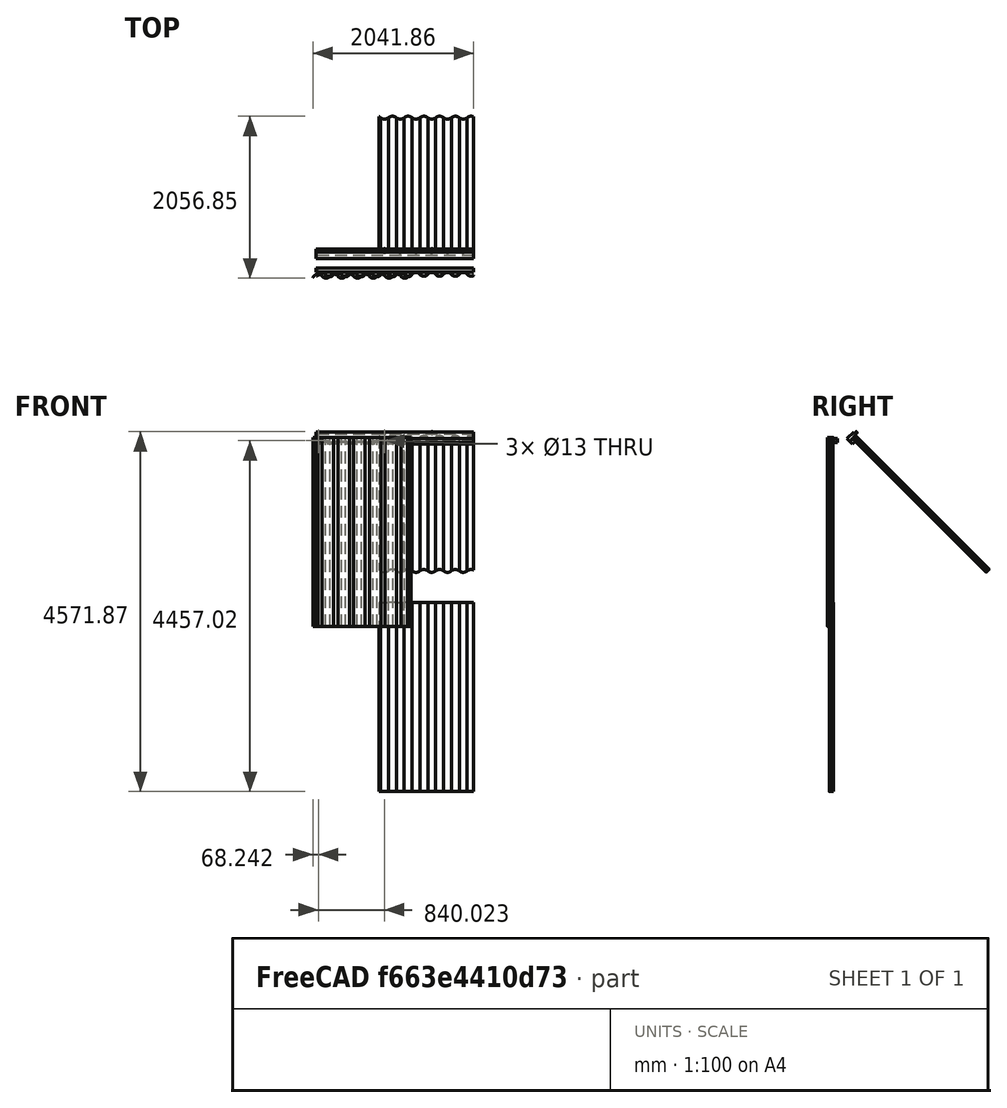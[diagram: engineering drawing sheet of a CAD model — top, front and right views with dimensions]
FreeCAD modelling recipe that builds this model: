
FCSTD DOCUMENT  (FreeCAD 0.17R11732 (Git))
Label: telhas
License: All rights reserved
LicenseURL: http://en.wikipedia.org/wiki/All_rights_reserved
objects: Part::FeaturePython×29, Part::Mirroring×3, App::FeaturePython×2, Part::Part2DObjectPython×2, Part::Feature×1, Part::Sweep×1
note: 36 computed .brp shape members not serialized (recipe doc carries the construction recipe); baked Part::Feature solids carry a one-line shape summary decoded from their .brp

FEATURE [Part::FeaturePython] Panel  # WARN: FeaturePython — macro-defined, semantics opaque (R4)
  Area = 2880000
  FaceMaker = 0
  HorizontalArea = 0
  Length = 1200
  MoveWithHost = false
  Normal = (0,0,0)
  PerimeterLength = 0
  Placement = pos=(-841.859,-100,-100) rot=(1,0,0;1.5708rad)
  Role = 0
  Sheets = 1
  Thickness = 5
  VerticalArea = 0
  WaveDirection = 0
  WaveHeight = 25
  WaveLength = 100
  WaveType = 0
  Width = 2400
FEATURE [Part::FeaturePython] Panel001  # WARN: FeaturePython — macro-defined, semantics opaque (R4)
  Area = 2880000
  CloneOf = -> Panel
  FaceMaker = 0
  HorizontalArea = 0
  Length = 1200
  MoveWithHost = false
  Normal = (0,0,0)
  PerimeterLength = 0
  Placement = pos=(-795.762,-82.2313,-100) rot=(1,0,0;1.5708rad)
  Role = 0
  Sheets = 1
  Thickness = 5
  VerticalArea = 0
  WaveDirection = 0
  WaveHeight = 0
  WaveLength = 0
  WaveType = 0
  Width = 2400
FEATURE [Part::FeaturePython] Panel002  # WARN: FeaturePython — macro-defined, semantics opaque (R4)
  Area = 2880000
  CloneOf = -> Panel
  FaceMaker = 0
  HorizontalArea = 0
  Length = 1200
  MoveWithHost = false
  Normal = (0,0,0)
  PerimeterLength = 0
  Placement = pos=(0,-76.1633,-2200) rot=(1,0,0;1.5708rad)
  Role = 0
  Sheets = 1
  Thickness = 5
  VerticalArea = 0
  WaveDirection = 0
  WaveHeight = 0
  WaveLength = 0
  WaveType = 0
  Width = 2400
FEATURE [App::FeaturePython] Dimension  # Draft dimension (typed FeaturePython)
  Diameter = false
  Dimline = (-800,-6.55651e-05,-1100)
  Direction = (0,0,0)
  Distance = 300
  End = (-600,-5.96046e-05,-1000)
  Normal = (0,-1,5.9605e-08)
  Start = (-600,-7.7486e-05,-1300)
FEATURE [Part::FeaturePython] Structure  # WARN: FeaturePython — macro-defined, semantics opaque (R4)
  FaceMaker = 0
  Height = 50
  HorizontalArea = 100000
  Length = 2000
  MoveWithHost = false
  Nodes = (2) [(0,0,9.71445e-17),(0,0,2000)]
  NodesOffset = 0
  Normal = (0,0,0)
  PerimeterLength = 4100
  Placement = pos=(600,-28.9872,1057.25) rot=(0,0,1;0rad)
  Role = 1
  VerticalArea = 205000
  Width = 50
FEATURE [Part::FeaturePython] Screw  label="M10x45-Screw"  # Fasteners workbench fastener (typed FeaturePython)
  Placement = pos=(-778.628,-86.0598,1057.25) rot=(1,0,0;1.5708rad)
  diameter = 10
  invert = false
  length = 8
  matchOuter = false
  offset = 0
  thread = false
  type = 4
FEATURE [Part::FeaturePython] Washer  label="M12-Washer"  # Fasteners workbench fastener (typed FeaturePython)
  Placement = pos=(-778.438,-84.9295,1057.02) rot=(-1,0,0;1.5708rad)
  diameter = 10
  invert = false
  matchOuter = false
  offset = 0
  type = 0
FEATURE [Part::FeaturePython] Clone  label="M12-Washer001"  # Draft clone (typed FeaturePython)
  AttacherType = Attacher::AttachEngine3D
  Objects = -> [Washer]
  Placement = pos=(-778.438,-74.5532,1057.02) rot=(-1,0,0;1.5708rad)
  Scale = (1,1,1)
FEATURE [Part::FeaturePython] Clone001  label="M10x45-Screw001"  # Draft clone (typed FeaturePython)
  AttacherType = Attacher::AttachEngine3D
  Objects = -> [Screw]
  Placement = pos=(-533.784,-86.0598,1057.25) rot=(1,0,0;1.5708rad)
  Scale = (1,1,1)
FEATURE [Part::FeaturePython] Clone002  label="M12-Washer002"  # Draft clone (typed FeaturePython)
  AttacherType = Attacher::AttachEngine3D
  Objects = -> [Washer]
  Placement = pos=(-533.595,-84.9295,1057.02) rot=(-1,0,0;1.5708rad)
  Scale = (1,1,1)
FEATURE [Part::FeaturePython] Clone003  label="M12-Washer003"  # Draft clone (typed FeaturePython)
  AttacherType = Attacher::AttachEngine3D
  Objects = -> [Clone]
  Placement = pos=(-533.595,-74.5532,1057.02) rot=(-1,0,0;1.5708rad)
  Scale = (1,1,1)
FEATURE [Part::FeaturePython] Clone004  label="M12-Washer004"  # Draft clone (typed FeaturePython)
  AttacherType = Attacher::AttachEngine3D
  Objects = -> [Clone003]
  Placement = pos=(-533.595,-56.9252,1057.02) rot=(-1,0,0;1.5708rad)
  Scale = (1,1,1)
FEATURE [Part::Feature] Face
  Placement = pos=(0,-807.107,251.472) rot=(-1,0,0;0.785398rad)
  shape: bbox 1200 x 38.89 x 38.89 mm, 1 faces, 0 solids (baked)
FEATURE [Part::Part2DObjectPython] DWire  # Draft 2D object (typed FeaturePython)
  ChamferSize = 0
  Closed = false
  End = (0,300,1100)
  FilletRadius = 70
  Length = 535.641
  MakeFace = true
  Points = (3) [(0,-100,1100),(0,100,1300),(0,300,1100)]
  Start = (0,-100,1100)
  Subdivisions = 0
FEATURE [Part::Sweep] Sweep
  Frenet = false
  Placement = pos=(0,0,9.34473) rot=(0,0,1;0rad)
  Sections = -> [Face]
  Solid = false
  Spine = -> DWire [Edge1,Edge2,Edge3]
  Transition = 1
FEATURE [Part::FeaturePython] Panel003  # WARN: FeaturePython — macro-defined, semantics opaque (R4)
  Area = 2880000
  CloneOf = -> Panel
  FaceMaker = 0
  HorizontalArea = 0
  Length = 1200
  MoveWithHost = false
  Normal = (0,0,0)
  PerimeterLength = 0
  Placement = pos=(0,-857.107,251.472) rot=(1,0,0;0.785398rad)
  Role = 0
  Sheets = 1
  Thickness = 5
  VerticalArea = 0
  WaveDirection = 0
  WaveHeight = 0
  WaveLength = 0
  WaveType = 0
  Width = 2400
FEATURE [Part::Mirroring] mirror  label="Mirror of Panel003"
  Base = (0,100,1100)
  Normal = (0,-1,0)
  Source = -> Panel003
FEATURE [Part::FeaturePython] Structure001  # WARN: FeaturePython — macro-defined, semantics opaque (R4)
  FaceMaker = 0
  Height = 50
  HorizontalArea = 70710.7
  Length = 2000
  MoveWithHost = false
  Nodes = (2) [(0,0,9.71445e-17),(0,0,2000)]
  NodesOffset = 0
  Normal = (0,0,0)
  PerimeterLength = 4070.71
  Placement = pos=(600,9.3393,1048.77) rot=(-1,0,0;0.785398rad)
  Role = 1
  VerticalArea = 5000
  Width = 50
FEATURE [Part::Mirroring] mirror001  label="Mirror of Structure001"
  Base = (0,100,1100)
  Normal = (0,-1,0)
  Source = -> Structure001
FEATURE [Part::FeaturePython] Structure002  # WARN: FeaturePython — macro-defined, semantics opaque (R4)
  FaceMaker = 0
  Height = 50
  HorizontalArea = 70710.7
  Length = 2000
  MoveWithHost = false
  Nodes = (2) [(0,1.98952e-15,9.71445e-17),(0,1.98952e-15,2000)]
  NodesOffset = 0
  Normal = (0,0,0)
  PerimeterLength = 4070.71
  Placement = pos=(600,19.9459,1108.87) rot=(-1,0,0;0.785398rad)
  Role = 1
  VerticalArea = 12000
  Width = 120
FEATURE [Part::Mirroring] mirror002  label="Mirror of Structure002"
  Base = (0,100,1200)
  Normal = (0,-1,0)
  Source = -> Structure002
FEATURE [Part::Part2DObjectPython] DWire001  # Draft 2D object (typed FeaturePython)
  ChamferSize = 0
  Closed = true
  End = (0,-100,700)
  FilletRadius = 0
  Length = 2097.06
  MakeFace = true
  Points = (6) [(0,-300,700),(0,100,1100),(0,500,700),(0,300,700),(0,100,900),(0,-100,700)]
  Start = (0,-300,700)
  Subdivisions = 0
FEATURE [Part::FeaturePython] Clone005  label="M12-Washer005"  # Draft clone (typed FeaturePython)
  AttacherType = Attacher::AttachEngine3D
  Objects = -> [Clone003]
  Placement = pos=(-533.595,-28.832,1154.33) rot=(1,0,0;3.92699rad)
  Scale = (1,1,1)
FEATURE [Part::FeaturePython] Clone006  label="M12-Washer006"  # Draft clone (typed FeaturePython)
  AttacherType = Attacher::AttachEngine3D
  Objects = -> [Clone002]
  Placement = pos=(-533.595,-36.1691,1161.67) rot=(1,0,0;3.92699rad)
  Scale = (1,1,1)
FEATURE [Part::FeaturePython] Clone007  label="M10x45-Screw002"  # Draft clone (typed FeaturePython)
  AttacherType = Attacher::AttachEngine3D
  Objects = -> [Clone001]
  Placement = pos=(-533.784,-36.8058,1162.63) rot=(1,0,0;0.785398rad)
  Scale = (1,1,1)
FEATURE [Part::FeaturePython] Clone008  label="M12-Washer007"  # Draft clone (typed FeaturePython)
  AttacherType = Attacher::AttachEngine3D
  Objects = -> [Clone005]
  Placement = pos=(68.1881,-28.832,1154.33) rot=(1,0,0;3.92699rad)
  Scale = (1,1,1)
FEATURE [Part::FeaturePython] Clone009  label="M12-Washer008"  # Draft clone (typed FeaturePython)
  AttacherType = Attacher::AttachEngine3D
  Objects = -> [Clone006]
  Placement = pos=(68.1881,-36.1691,1161.67) rot=(1,0,0;3.92699rad)
  Scale = (1,1,1)
FEATURE [Part::FeaturePython] Clone010  label="M10x45-Screw003"  # Draft clone (typed FeaturePython)
  AttacherType = Attacher::AttachEngine3D
  Objects = -> [Clone007]
  Placement = pos=(67.9986,-36.8058,1162.63) rot=(1,0,0;0.785398rad)
  Scale = (1,1,1)
FEATURE [Part::FeaturePython] Clone011  label="M12-Washer009"  # Draft clone (typed FeaturePython)
  AttacherType = Attacher::AttachEngine3D
  Objects = -> [Clone005]
  Placement = pos=(70.6321,228.832,1154.33) rot=(0,0.92388,-0.382683;3.14159rad)
  Scale = (1,1,1)
FEATURE [Part::FeaturePython] Clone012  label="M12-Washer010"  # Draft clone (typed FeaturePython)
  AttacherType = Attacher::AttachEngine3D
  Objects = -> [Clone008]
  Placement = pos=(-531.151,228.832,1154.33) rot=(0,0.92388,-0.382683;3.14159rad)
  Scale = (1,1,1)
FEATURE [Part::FeaturePython] Clone013  label="M10x45-Screw004"  # Draft clone (typed FeaturePython)
  AttacherType = Attacher::AttachEngine3D
  Objects = -> [Clone010]
  Placement = pos=(-530.961,236.806,1162.63) rot=(0,0.382683,0.92388;3.14159rad)
  Scale = (1,1,1)
FEATURE [Part::FeaturePython] Clone014  label="M12-Washer011"  # Draft clone (typed FeaturePython)
  AttacherType = Attacher::AttachEngine3D
  Objects = -> [Clone006]
  Placement = pos=(70.6321,236.169,1161.67) rot=(0,0.92388,-0.382683;3.14159rad)
  Scale = (1,1,1)
FEATURE [Part::FeaturePython] Clone015  label="M12-Washer012"  # Draft clone (typed FeaturePython)
  AttacherType = Attacher::AttachEngine3D
  Objects = -> [Clone009]
  Placement = pos=(-531.151,236.169,1161.67) rot=(0,0.92388,-0.382683;3.14159rad)
  Scale = (1,1,1)
FEATURE [Part::FeaturePython] Clone016  label="M10x45-Screw005"  # Draft clone (typed FeaturePython)
  AttacherType = Attacher::AttachEngine3D
  Objects = -> [Clone007]
  Placement = pos=(70.8217,236.806,1162.63) rot=(0,0.382683,0.92388;3.14159rad)
  Scale = (1,1,1)
FEATURE [Part::FeaturePython] Clone017  label="M10x45-Screw006"  # Draft clone (typed FeaturePython)
  AttacherType = Attacher::AttachEngine3D
  Objects = -> [Screw]
  Placement = pos=(-1373.81,-86.0598,1057.25) rot=(1,0,0;1.5708rad)
  Scale = (1,1,1)
FEATURE [Part::FeaturePython] Clone018  label="M12-Washer013"  # Draft clone (typed FeaturePython)
  AttacherType = Attacher::AttachEngine3D
  Objects = -> [Washer]
  Placement = pos=(-1373.62,-84.9295,1057.02) rot=(-1,0,0;1.5708rad)
  Scale = (1,1,1)
FEATURE [Part::FeaturePython] Clone019  label="M12-Washer014"  # Draft clone (typed FeaturePython)
  AttacherType = Attacher::AttachEngine3D
  Objects = -> [Clone]
  Placement = pos=(-1373.62,-74.5532,1057.02) rot=(-1,0,0;1.5708rad)
  Scale = (1,1,1)
FEATURE [App::FeaturePython] Dimension001  # Draft dimension (typed FeaturePython)
  Diameter = false
  Dimline = (-1271.27,7.47042e-05,1253.33)
  Direction = (0,0,0)
  Distance = 41.8595
  End = (-1400,6.55651e-05,1100)
  Normal = (0,-1,5.9605e-08)
  Start = (-1441.86,6.55651e-05,1100)
